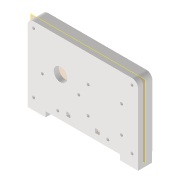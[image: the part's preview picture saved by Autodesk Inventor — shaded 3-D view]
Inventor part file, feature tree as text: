
AUTODESK INVENTOR PART (.ipt)
format: ipt  version: 2022 (Build 260153000, 153)  size: 455,168 bytes
history: native  units: mm
features: reference x15, sketch x11, extrude x9, other x9, projected_geometry x7, plane x3, hole x2, fillet x1
ambient origin geometry x8: Origin, YZ Plane, XZ Plane, XY Plane, X Axis, Y Axis, Z Axis, Center Point
bodies: Volumenkörper1 (feature_tree)
feature tree (57):
  plane  "Arbeitsebene1"
  sketch  "Skizze1"  dims[d0=3.0mm d1=3.0mm d2=0.0mm]
  plane  "Arbeitsebene2"
  extrude  "Extrusion1"  Depth=3.0mm TaperAngle=0.0deg
  extrude  "Extrusion2"  Depth=2.8mm
  extrude  "Extrusion3"  Depth=10.0mm
  extrude  "Extrusion4"  Depth=9.0mm
  extrude  "Extrusion5"  Depth=2.5mm TaperAngle=0.0deg
  extrude  "Extrusion6"  Depth=2.8mm
  extrude  "Extrusion7"  Depth=15.0mm
  sketch  "Skizze8"  dims[d19=7.0mm d20=0.0mm d21=10.0mm d22=0.0mm]
  plane  "Arbeitsebene3"
  extrude  "Extrusion8"  Depth=10.0mm TaperAngle=0.0deg
  extrude  "Extrusion9"  Depth=10.0mm TaperAngle=0.0deg
  hole  "Bohrung1"  [1 undecoded]
  hole  "Bohrung2"  [1 undecoded]
  fillet  "Rundung1"  Radius=10.0mm
  reference  "Referenz1"
  sketch  "Skizze2"  dims[d3=2.8mm d4=2.8mm]
  reference  "Referenz2"
  reference  "Referenz3"
  sketch  "Skizze3"  dims[d5=10.0mm d6=0.0mm d7=0.5mm]
  reference  "Referenz4"
  projected_geometry  "Projizierte Kontur1"
  sketch  "Skizze4"  dims[d8=9.0mm d9=0.0mm d10=7.5mm]
  reference  "Referenz5"
  reference  "Referenz6"
  sketch  "Skizze5"  dims[d11=9.0mm d12=-0.523599mm d13=2.5mm d14=0.0mm]
  projected_geometry  "Projizierte Kontur2"
  reference  "Referenz7"
  reference  "Referenz8"
  sketch  "Skizze6"  dims[d15=2.8mm d16=2.8mm]
  projected_geometry  "Projizierte Kontur3"
  sketch  "Skizze7"  dims[d17=103.0mm d18=15.0mm]
  reference  "Referenz9"
  reference  "Referenz10"
  reference  "Referenz11"
  reference  "Referenz12"
  reference  "Referenz13"
  projected_geometry  "Projizierte Kontur4"
  sketch  "Skizze9"  dims[d23=5.0mm d24=10.0mm d25=0.0mm]
  projected_geometry  "Projizierte Kontur5"
  projected_geometry  "Projizierte Kontur6"
  reference  "Referenz14"
  sketch  "Skizze10"  dims[d26=2.8mm d27=2.8mm]
  reference  "Referenz15"
  sketch  "Skizze11"  dims[d28=10.0mm d29=0.0mm d30=2.8mm d31=20.0mm d33=100.0mm d34=10.0mm d36=10.0mm d38=32.0mm d39=26.0mm d40=2.8mm d41=6.0mm d42=4.0mm d43=2.0mm d44=90.0deg d45=14.0mm d46=20.594885mm d47=2.8mm d48=6.0mm d49=4.0mm d50=2.0mm d51=90.0deg d52=14.0mm d53=20.594885mm d54=2.0mm]
  projected_geometry  "Projizierte Kontur7"
  other  "Assembly_Cassete_Deck.iam"
  other  "00_Cassette:1"
  parser-record x4  (decoder bookkeeping rows leaked as tree rows — omitted from the tree; the rows remain in map.json)
  other  "00_Stepper_Motor_28BYJ-48:1"
  other  "10_Base_puzzle_v3:3"
  other  "Baugruppe3"
note: 2 required parameter values undecoded (feature->parameter linkage not recoverable at this tier; creation-order binding heuristic only, values carry confidence <= 0.55)
